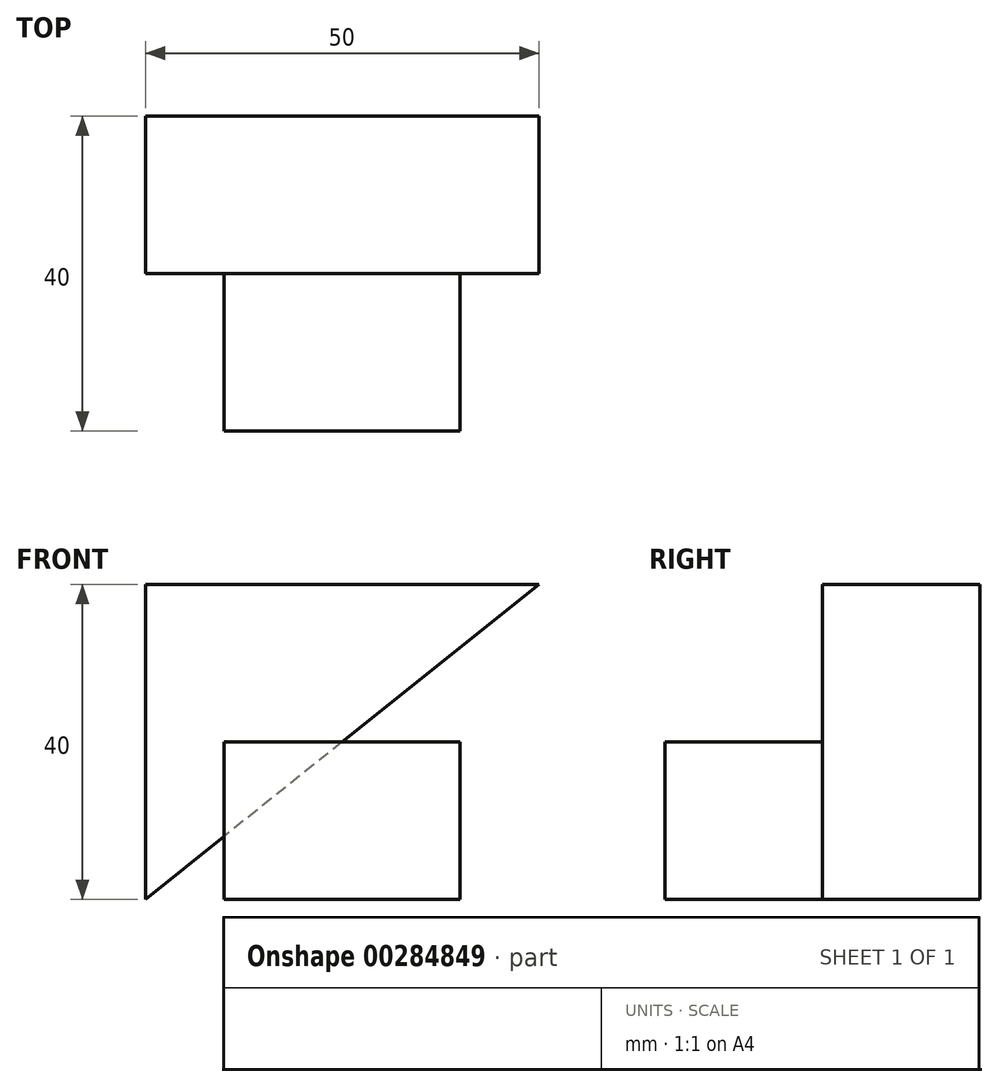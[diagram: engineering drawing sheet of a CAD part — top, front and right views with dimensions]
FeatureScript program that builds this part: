
annotation { "Feature Type Name" : "Feature", "Feature Type Description" : "" }
export const myFeature = defineFeature(function(context is Context, id is Id, definition is map)
    precondition{}
    {
        {
            var Q0;
            Q0=qCreatedBy(makeId("Front.planeOp"),FACE);
            var sketch = newSketch(context, id + "F0", { "sketchPlane" : qUnion([Q0])});
            skLineSegment(sketch, "E0.bottom", {"start": v(0, 0) * mm, "end": v(50, 0) * mm});
            skLineSegment(sketch, "E0.top", {"start": v(0, 40) * mm, "end": v(50, 40) * mm});
            skLineSegment(sketch, "E0.left", {"start": v(0, 0) * mm, "end": v(0, 40) * mm});
            skLineSegment(sketch, "E0.right", {"start": v(50, 0) * mm, "end": v(50, 40) * mm});
            skLineSegment(sketch, "E1", {"start": v(50, 40) * mm, "end": v(0, 0) * mm});
            skSolve(sketch);
        }
        {
            var Q0;
            Q0=makeQuery(id+"F0.imprint","IMPRINT",FACE,{"disambiguationData":[TD([[makeQuery(id+"F0.imprint","IMPRINT",EDGE,{"derivedFrom":sQuery(id+"F0.wireOp",EDGE,"E0.top")}),-1.0]])]});
            extrude(context, id + "F1", {"entities" : qUnion([Q0]), "depth" : 20 * mm});
        }
        {
            var Q0;
            Q0=makeQuery(id+"F1.opExtrude","CAP_FACE",FACE,{"disambiguationData":[OSD([sQuery(id+"F0.wireOp",EDGE,"E0.bottom"),sQuery(id+"F0.wireOp",EDGE,"E0.top"),sQuery(id+"F0.wireOp",EDGE,"E0.left"),sQuery(id+"F0.wireOp",EDGE,"E0.right")])],"isStart":false});
            var sketch = newSketch(context, id + "F2", { "sketchPlane" : qUnion([Q0])});
            skLineSegment(sketch, "E2.bottom", {"start": v(10, 0) * mm, "end": v(40, 0) * mm});
            skLineSegment(sketch, "E2.top", {"start": v(10, 20) * mm, "end": v(40, 20) * mm});
            skLineSegment(sketch, "E2.left", {"start": v(10, 0) * mm, "end": v(10, 20) * mm});
            skLineSegment(sketch, "E2.right", {"start": v(40, 0) * mm, "end": v(40, 20) * mm});
            skSolve(sketch);
        }
        {
            var Q0;
            Q0=qSketchRegion(id+"F2",true);
            extrude(context, id + "F3", {"entities" : qUnion([Q0]), "operationType" : NewBodyOperationType.ADD, "depth" : 20 * mm});
        }
    });
